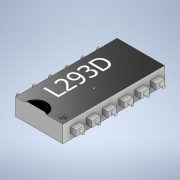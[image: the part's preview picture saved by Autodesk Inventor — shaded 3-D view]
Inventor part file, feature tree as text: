
AUTODESK INVENTOR PART (.ipt)
format: ipt  version: 2021 (Build 250183000, 183)  size: 250,880 bytes
history: native  units: mm
features: sketch x9, extrude x7, hole x1, fillet x1
ambient origin geometry x8: Origin, YZ Plane, XZ Plane, XY Plane, X Axis, Y Axis, Z Axis, Center Point
bodies: Solid1 (feature_tree)
feature tree (18):
  extrude  "Extrusion1"  Depth=28.0mm
  extrude  "Extrusion2"  Depth=10.0mm
  extrude  "Extrusion3"  Depth=3.5mm
  extrude  "Extrusion4"  Depth=5.0mm
  extrude  "Extrusion5"  Depth=5.0mm
  extrude  "Extrusion6"  Depth=5.0mm
  hole  "Hole1"  [1 undecoded]
  extrude  "Extrusion7"  Depth=3.5mm
  fillet  "Fillet1"  Radius=1.7mm
  sketch  "Sketch9"  dims[d20=1.7mm d21=1.7mm d22=1.7mm d23=1.7mm d24=2.0mm d25=0.0mm d26=5.0mm d27=0.0mm d28=2.0mm d29=0.0mm d30=4.0mm d31=6.0mm d32=4.0mm d33=2.0mm d34=90.0deg d35=2.0mm d36=0.0mm d37=1.0mm d38=0.0mm d39=2.0mm]
  sketch  "Sketch1"  dims[d0=60.0mm d1=28.0mm]
  sketch  "Sketch2"  dims[d2=10.0mm d3=0.0mm d4=10.0mm]
  sketch  "Sketch3"  dims[d5=3.0mm d6=3.5mm]
  sketch  "Sketch4"  dims[d7=3.5mm d8=5.0mm]
  sketch  "Sketch5"  dims[d9=5.0mm d10=5.0mm]
  sketch  "Sketch6"  dims[d11=5.0mm d12=5.0mm]
  sketch  "Sketch7"  dims[d13=5.0mm d14=3.5mm d15=0.0mm]
  sketch  "Sketch8"  dims[d16=3.5mm d17=0.0mm d18=1.7mm d19=1.7mm]
note: 1 required parameter value undecoded (feature->parameter linkage not recoverable at this tier; creation-order binding heuristic only, values carry confidence <= 0.55)
